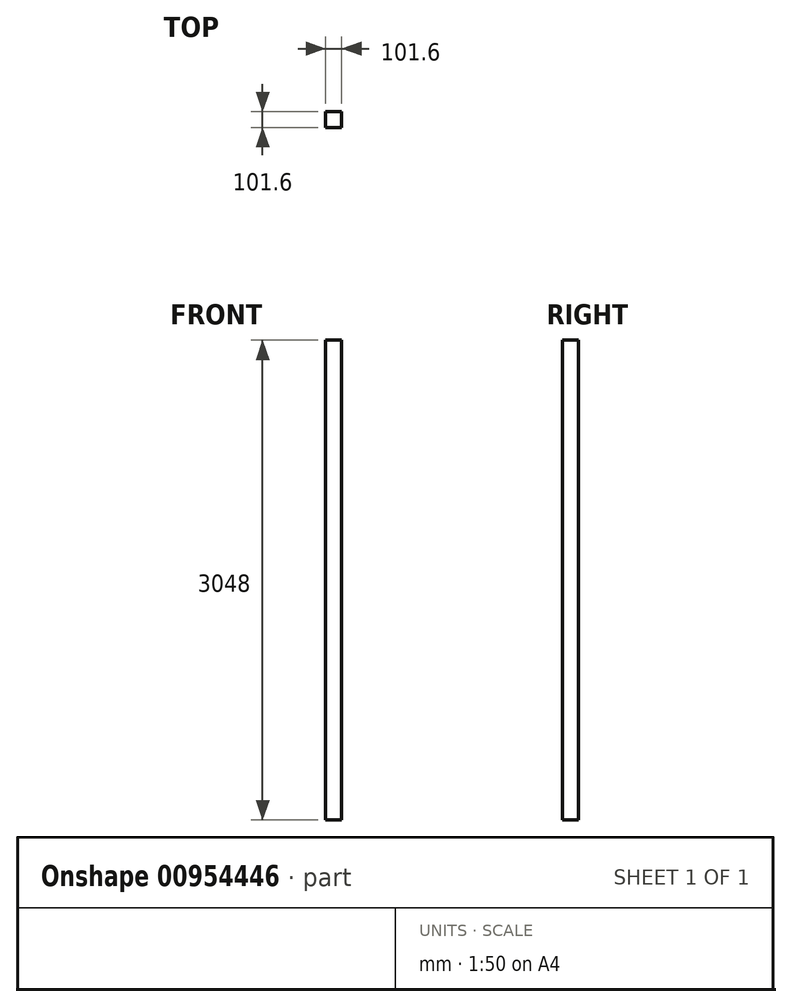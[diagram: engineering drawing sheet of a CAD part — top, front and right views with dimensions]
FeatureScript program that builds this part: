
annotation { "Feature Type Name" : "Feature", "Feature Type Description" : "" }
export const myFeature = defineFeature(function(context is Context, id is Id, definition is map)
    precondition{}
    {
        {
            var Q0;
            Q0=qCreatedBy(makeId("Top.planeOp"),FACE);
            var sketch = newSketch(context, id + "F0", { "sketchPlane" : qUnion([Q0])});
            skLineSegment(sketch, "E0.bottom", {"start": v(0, 0) * mm, "end": v(101.6, 0) * mm});
            skLineSegment(sketch, "E0.top", {"start": v(0, 101.6) * mm, "end": v(101.6, 101.6) * mm});
            skLineSegment(sketch, "E0.left", {"start": v(0, 0) * mm, "end": v(0, 101.6) * mm});
            skLineSegment(sketch, "E0.right", {"start": v(101.6, 0) * mm, "end": v(101.6, 101.6) * mm});
            skSolve(sketch);
        }
        {
            var Q0;
            Q0 = qSketchRegion(id + "F0", true);
            extrude(context, id + "F1", {"entities" : qUnion([Q0]), "depth" : 3048 * mm, "offsetDistance" : 25.4 * mm});
        }
    });
